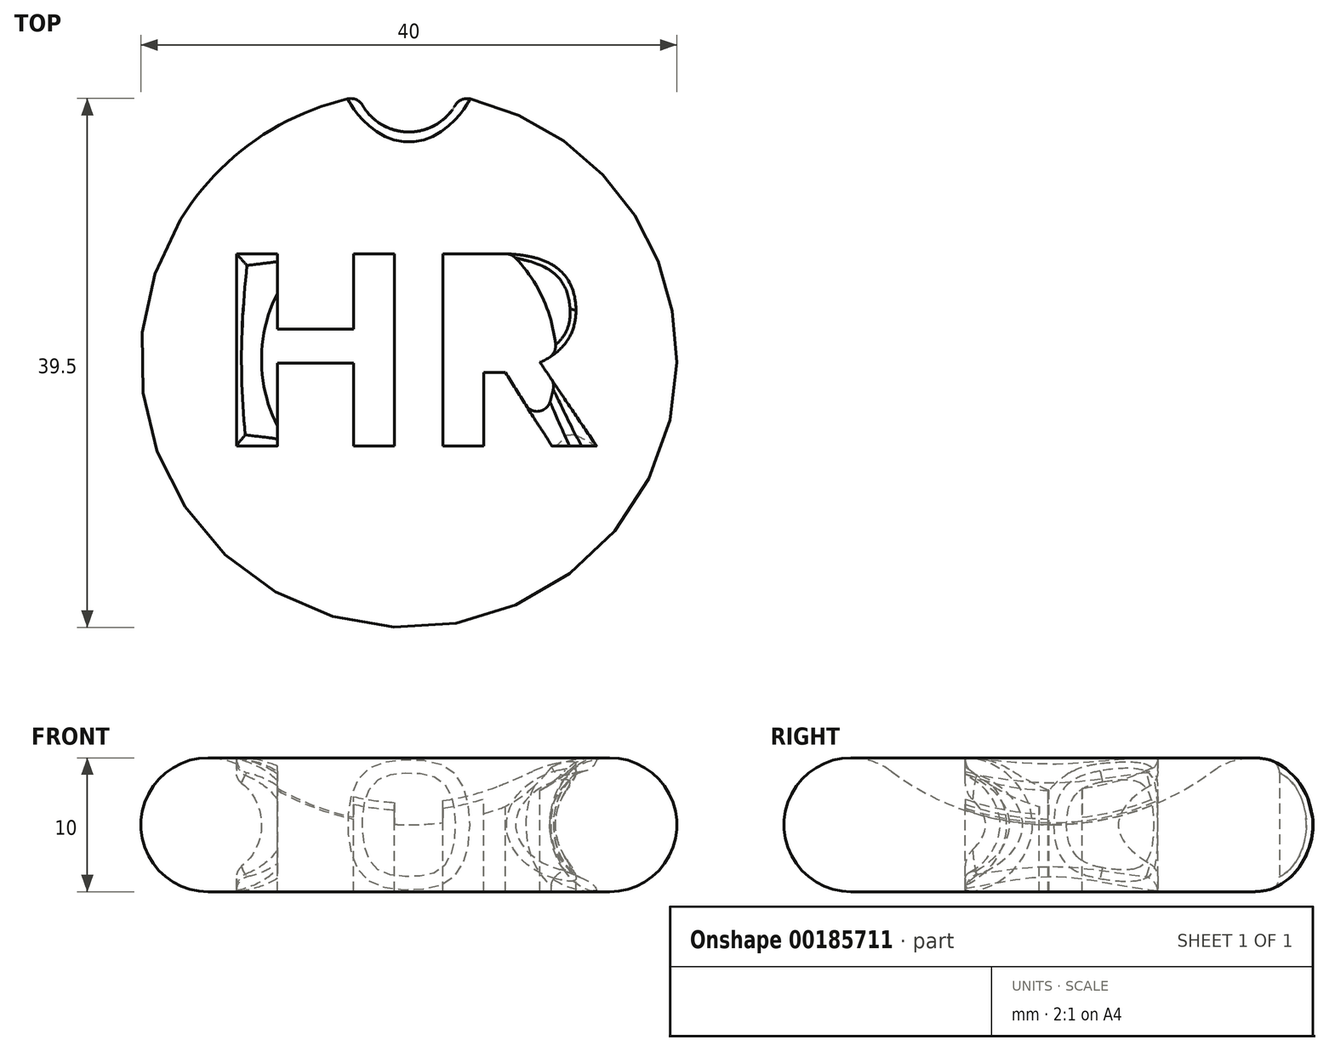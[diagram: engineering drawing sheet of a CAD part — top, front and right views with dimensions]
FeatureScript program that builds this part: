
annotation { "Feature Type Name" : "Feature", "Feature Type Description" : "" }
export const myFeature = defineFeature(function(context is Context, id is Id, definition is map)
    precondition{}
    {
        {
            var Q0;
            Q0=qCreatedBy(makeId("Front.planeOp"),FACE);
            var sketch = newSketch(context, id + "F0", { "sketchPlane" : qUnion([Q0])});
            skArc(sketch, "E0", {"start": v(-12, 9) * mm, "mid": v(-19.74, 6.58) * mm, "end": v(-15, 0) * mm});
            skArc(sketch, "E1", {"start": v(-12, 9) * mm, "mid": v(-6.32, 6.03) * mm, "end": v(0, 5) * mm});
            skLineSegment(sketch, "E2", {"start": v(0, 0) * mm, "end": v(-15, 0) * mm});
            skLineSegment(sketch, "E3", {"start": v(0, 0) * mm, "end": v(0, 5) * mm});
            skSolve(sketch);
        }
        {
            var Q0;
            Q0=makeQuery(id+"F0.imprint","IMPRINT",FACE,{"disambiguationData":[TD([[makeQuery(id+"F0.imprint","IMPRINT",EDGE,{"derivedFrom":sQuery(id+"F0.wireOp",EDGE,"E0")}),1.0]])]});
            var Q1;
            Q1=sQuery(id+"F0.wireOp",EDGE,"E3");
            revolve(context, id + "F1", {"entities" : qUnion([Q0]), "axis" : qUnion([Q1]), "revolveType" : RevolveType.FULL});
        }
        {
            var Q0;
            Q0=qCreatedBy(makeId("Top.planeOp"),FACE);
            cPlane(context, id + "F2", {"entities" : qUnion([Q0]), "cplaneType" : CPlaneType.OFFSET, "offset" : 10 * mm, "width" : 150 * mm, "height" : 150 * mm});
        }
        {
            var Q0;
            Q0=qCreatedBy(id+"F2.planeOp",FACE);
            var sketch = newSketch(context, id + "F3", { "sketchPlane" : qUnion([Q0])});
            skText(sketch, "E4", { "text": "HR", "fontName": "OpenSans-Bold.ttf"});
            const initialGuessF3  = {"E4": [-0.01468, -0.00647, 1, 0, 0.0145]};
            skSetInitialGuess(sketch, initialGuessF3);
            skSolve(sketch);
        }
        {
            var Q0;
            Q0 = qSketchRegion(id + "F3", true);
            extrude(context, id + "F4", {"entities" : qUnion([Q0]), "operationType" : NewBodyOperationType.REMOVE, "oppositeDirection" : true, "depth" : 25 * mm});
        }
        {
            var Q0;
            Q0=makeQuery(id+"F3.imprint","IMPRINT",FACE,{"disambiguationData":[TD([[makeQuery(id+"F3.imprint","IMPRINT",EDGE,{"derivedFrom":sQuery(id+"F3.wireOp",EDGE,"E4.sketch_text.stroke-12")}),1.0]])]});
            extrude(context, id + "F5", {"entities" : qUnion([Q0]), "operationType" : NewBodyOperationType.REMOVE, "oppositeDirection" : true, "depth" : 25 * mm});
        }
        {
            var Q0;
            Q0=qCreatedBy(makeId("Front.planeOp"),FACE);
            var sketch = newSketch(context, id + "F6", { "sketchPlane" : qUnion([Q0])});
            skCircle(sketch, "E5.0", {"center": v(-15, 5) * mm, "radius": 4 * mm});
            skSolve(sketch);
        }
        {
            var Q0;
            Q0=makeQuery(id+"F6.imprint","IMPRINT",FACE,{"disambiguationData":[TD([[makeQuery(id+"F6.imprint","IMPRINT",EDGE,{"derivedFrom":sQuery(id+"F6.wireOp",EDGE,"E5.0")}),1.0]])]});
            var Q1;
            Q1=sQuery(id+"F0.wireOp",EDGE,"E3");
            revolve(context, id + "F7", {"operationType" : NewBodyOperationType.ADD, "entities" : qUnion([Q0]), "axis" : qUnion([Q1]), "revolveType" : RevolveType.FULL});
        }
        {
            var Q0;
            Q0=qCreatedBy(makeId("Top.planeOp"),FACE);
            var sketch = newSketch(context, id + "F8", { "sketchPlane" : qUnion([Q0])});
            skCircle(sketch, "E6", {"center": v(0, 21) * mm, "radius": 4 * mm});
            skSolve(sketch);
        }
        {
            var Q0;
            Q0=makeQuery(id+"F8.imprint","IMPRINT",FACE,{"disambiguationData":[TD([[makeQuery(id+"F8.imprint","IMPRINT",EDGE,{"derivedFrom":sQuery(id+"F8.wireOp",EDGE,"E6")}),1.0]])]});
            extrude(context, id + "F9", {"entities" : qUnion([Q0]), "operationType" : NewBodyOperationType.REMOVE, "depth" : 23.3 * mm});
        }
        {
            var Q0;
            Q0=makeQuery(id+"F9.boolean.opBoolean","INTERSECT",EDGE,{"derivedFrom":[makeQuery(id+"F4.boolean.opBoolean","SPLIT",FACE,{"disambiguationData":[TD([makeQuery(id+"F1.opRevolve","SWEPT_FACE",FACE,{"disambiguationData":[OSD([sQuery(id+"F0.wireOp",EDGE,"E2")])]})])],"derivedFrom":makeQuery(id+"F1.opRevolve","SWEPT_FACE",FACE,{"disambiguationData":[OSD([sQuery(id+"F0.wireOp",EDGE,"E0")])]})}),makeQuery(id+"F9.opExtrude","SWEPT_FACE",FACE,{"disambiguationData":[OSD([sQuery(id+"F8.wireOp",EDGE,"E6")])]})]});
            fillet(context, id + "F10", {"entities" : qUnion([Q0]), "radius" : 1 * mm, "tangentPropagation" : true, "allowEdgeOverflow" : false});
        }
        {
            var Q0;
            Q0=makeQuery(id+"F7.boolean.opBoolean","INTERSECT",EDGE,{"disambiguationData":[OD(0.0)],"derivedFrom":[makeQuery(id+"F4.boolean.opBoolean","COPY",FACE,{"derivedFrom":makeQuery(id+"F4.opExtrude","SWEPT_FACE",FACE,{"disambiguationData":[OSD([sQuery(id+"F3.wireOp",EDGE,"E4.sketch_text.stroke-5")])]})}),makeQuery(id+"F7.opRevolve","SWEPT_FACE",FACE,{"disambiguationData":[OSD([sQuery(id+"F6.wireOp",EDGE,"E5.0")])]})]});
            var Q1;
            Q1=makeQuery(id+"F7.boolean.opBoolean","INTERSECT",EDGE,{"disambiguationData":[OD(0.0)],"derivedFrom":[makeQuery(id+"F4.boolean.opBoolean","COPY",FACE,{"derivedFrom":makeQuery(id+"F4.opExtrude","SWEPT_FACE",FACE,{"disambiguationData":[OSD([sQuery(id+"F3.wireOp",EDGE,"E4.sketch_text.stroke-6")])]})}),makeQuery(id+"F7.opRevolve","SWEPT_FACE",FACE,{"disambiguationData":[OSD([sQuery(id+"F6.wireOp",EDGE,"E5.0")])]})]});
            var Q2;
            Q2=makeQuery(id+"F7.boolean.opBoolean","INTERSECT",EDGE,{"disambiguationData":[OD(1.0)],"derivedFrom":[makeQuery(id+"F4.boolean.opBoolean","COPY",FACE,{"derivedFrom":makeQuery(id+"F4.opExtrude","SWEPT_FACE",FACE,{"disambiguationData":[OSD([sQuery(id+"F3.wireOp",EDGE,"E4.sketch_text.stroke-4")])]})}),makeQuery(id+"F7.opRevolve","SWEPT_FACE",FACE,{"disambiguationData":[OSD([sQuery(id+"F6.wireOp",EDGE,"E5.0")])]})]});
            fillet(context, id + "F11", {"entities" : qUnion([Q0, Q1, Q2]), "radius" : 1 * mm, "tangentPropagation" : true, "allowEdgeOverflow" : false});
        }
        {
            var Q0;
            Q0=makeQuery(id+"F7.boolean.opBoolean","INTERSECT",EDGE,{"disambiguationData":[OD(0.0)],"derivedFrom":[makeQuery(id+"F4.boolean.opBoolean","COPY",FACE,{"derivedFrom":makeQuery(id+"F4.opExtrude","SWEPT_FACE",FACE,{"disambiguationData":[OSD([sQuery(id+"F3.wireOp",EDGE,"E4.sketch_text.stroke-28")])]})}),makeQuery(id+"F7.opRevolve","SWEPT_FACE",FACE,{"disambiguationData":[OSD([sQuery(id+"F6.wireOp",EDGE,"E5.0")])]})]});
            var Q1;
            Q1=makeQuery(id+"F7.boolean.opBoolean","INTERSECT",EDGE,{"derivedFrom":[makeQuery(id+"F4.boolean.opBoolean","COPY",FACE,{"derivedFrom":makeQuery(id+"F4.opExtrude","SWEPT_FACE",FACE,{"disambiguationData":[OSD([sQuery(id+"F3.wireOp",EDGE,"E4.sketch_text.stroke-29")])]})}),makeQuery(id+"F7.opRevolve","SWEPT_FACE",FACE,{"disambiguationData":[OSD([sQuery(id+"F6.wireOp",EDGE,"E5.0")])]})]});
            var Q2;
            Q2=makeQuery(id+"F7.boolean.opBoolean","INTERSECT",EDGE,{"derivedFrom":[makeQuery(id+"F4.boolean.opBoolean","COPY",FACE,{"derivedFrom":makeQuery(id+"F4.opExtrude","SWEPT_FACE",FACE,{"disambiguationData":[OSD([sQuery(id+"F3.wireOp",EDGE,"E4.sketch_text.stroke-27")])]})}),makeQuery(id+"F7.opRevolve","SWEPT_FACE",FACE,{"disambiguationData":[OSD([sQuery(id+"F6.wireOp",EDGE,"E5.0")])]})]});
            var Q3;
            Q3=makeQuery(id+"F7.boolean.opBoolean","INTERSECT",EDGE,{"disambiguationData":[OD(1.0)],"derivedFrom":[makeQuery(id+"F4.boolean.opBoolean","COPY",FACE,{"derivedFrom":makeQuery(id+"F4.opExtrude","SWEPT_FACE",FACE,{"disambiguationData":[OSD([sQuery(id+"F3.wireOp",EDGE,"E4.sketch_text.stroke-25")])]})}),makeQuery(id+"F7.opRevolve","SWEPT_FACE",FACE,{"disambiguationData":[OSD([sQuery(id+"F6.wireOp",EDGE,"E5.0")])]})]});
            var Q4;
            Q4=makeQuery(id+"F7.boolean.opBoolean","INTERSECT",EDGE,{"derivedFrom":[makeQuery(id+"F4.boolean.opBoolean","COPY",FACE,{"derivedFrom":makeQuery(id+"F4.opExtrude","SWEPT_FACE",FACE,{"disambiguationData":[OSD([sQuery(id+"F3.wireOp",EDGE,"E4.sketch_text.stroke-26")])]})}),makeQuery(id+"F7.opRevolve","SWEPT_FACE",FACE,{"disambiguationData":[OSD([sQuery(id+"F6.wireOp",EDGE,"E5.0")])]})]});
            var Q5;
            Q5=makeQuery(id+"F7.boolean.opBoolean","INTERSECT",EDGE,{"disambiguationData":[OD(1.0)],"derivedFrom":[makeQuery(id+"F4.boolean.opBoolean","COPY",FACE,{"derivedFrom":makeQuery(id+"F4.opExtrude","SWEPT_FACE",FACE,{"disambiguationData":[OSD([sQuery(id+"F3.wireOp",EDGE,"E4.sketch_text.stroke-24")])]})}),makeQuery(id+"F7.opRevolve","SWEPT_FACE",FACE,{"disambiguationData":[OSD([sQuery(id+"F6.wireOp",EDGE,"E5.0")])]})]});
            var Q6;
            Q6=makeQuery(id+"F7.boolean.opBoolean","INTERSECT",EDGE,{"derivedFrom":[makeQuery(id+"F4.boolean.opBoolean","COPY",FACE,{"derivedFrom":makeQuery(id+"F4.opExtrude","SWEPT_FACE",FACE,{"disambiguationData":[OSD([sQuery(id+"F3.wireOp",EDGE,"E4.sketch_text.stroke-23")])]})}),makeQuery(id+"F7.opRevolve","SWEPT_FACE",FACE,{"disambiguationData":[OSD([sQuery(id+"F6.wireOp",EDGE,"E5.0")])]})]});
            fillet(context, id + "F12", {"entities" : qUnion([Q0, Q1, Q2, Q3, Q4, Q5, Q6]), "radius" : 1 * mm, "tangentPropagation" : true, "allowEdgeOverflow" : false});
        }
        {
            var Q0;
            Q0=makeQuery(id+"F7.boolean.opBoolean","INTERSECT",EDGE,{"disambiguationData":[OD(0.0)],"derivedFrom":[makeQuery(id+"F4.boolean.opBoolean","COPY",FACE,{"derivedFrom":makeQuery(id+"F4.opExtrude","SWEPT_FACE",FACE,{"disambiguationData":[OSD([sQuery(id+"F3.wireOp",EDGE,"E4.sketch_text.stroke-4")])]})}),makeQuery(id+"F7.opRevolve","SWEPT_FACE",FACE,{"disambiguationData":[OSD([sQuery(id+"F6.wireOp",EDGE,"E5.0")])]})]});
            var Q1;
            Q1=makeQuery(id+"F7.boolean.opBoolean","INTERSECT",EDGE,{"disambiguationData":[OD(1.0)],"derivedFrom":[makeQuery(id+"F4.boolean.opBoolean","COPY",FACE,{"derivedFrom":makeQuery(id+"F4.opExtrude","SWEPT_FACE",FACE,{"disambiguationData":[OSD([sQuery(id+"F3.wireOp",EDGE,"E4.sketch_text.stroke-5")])]})}),makeQuery(id+"F7.opRevolve","SWEPT_FACE",FACE,{"disambiguationData":[OSD([sQuery(id+"F6.wireOp",EDGE,"E5.0")])]})]});
            var Q2;
            Q2=makeQuery(id+"F7.boolean.opBoolean","INTERSECT",EDGE,{"disambiguationData":[OD(1.0)],"derivedFrom":[makeQuery(id+"F4.boolean.opBoolean","COPY",FACE,{"derivedFrom":makeQuery(id+"F4.opExtrude","SWEPT_FACE",FACE,{"disambiguationData":[OSD([sQuery(id+"F3.wireOp",EDGE,"E4.sketch_text.stroke-6")])]})}),makeQuery(id+"F7.opRevolve","SWEPT_FACE",FACE,{"disambiguationData":[OSD([sQuery(id+"F6.wireOp",EDGE,"E5.0")])]})]});
            fillet(context, id + "F13", {"entities" : qUnion([Q0, Q1, Q2]), "radius" : 1 * mm, "tangentPropagation" : true, "allowEdgeOverflow" : false});
        }
    });
